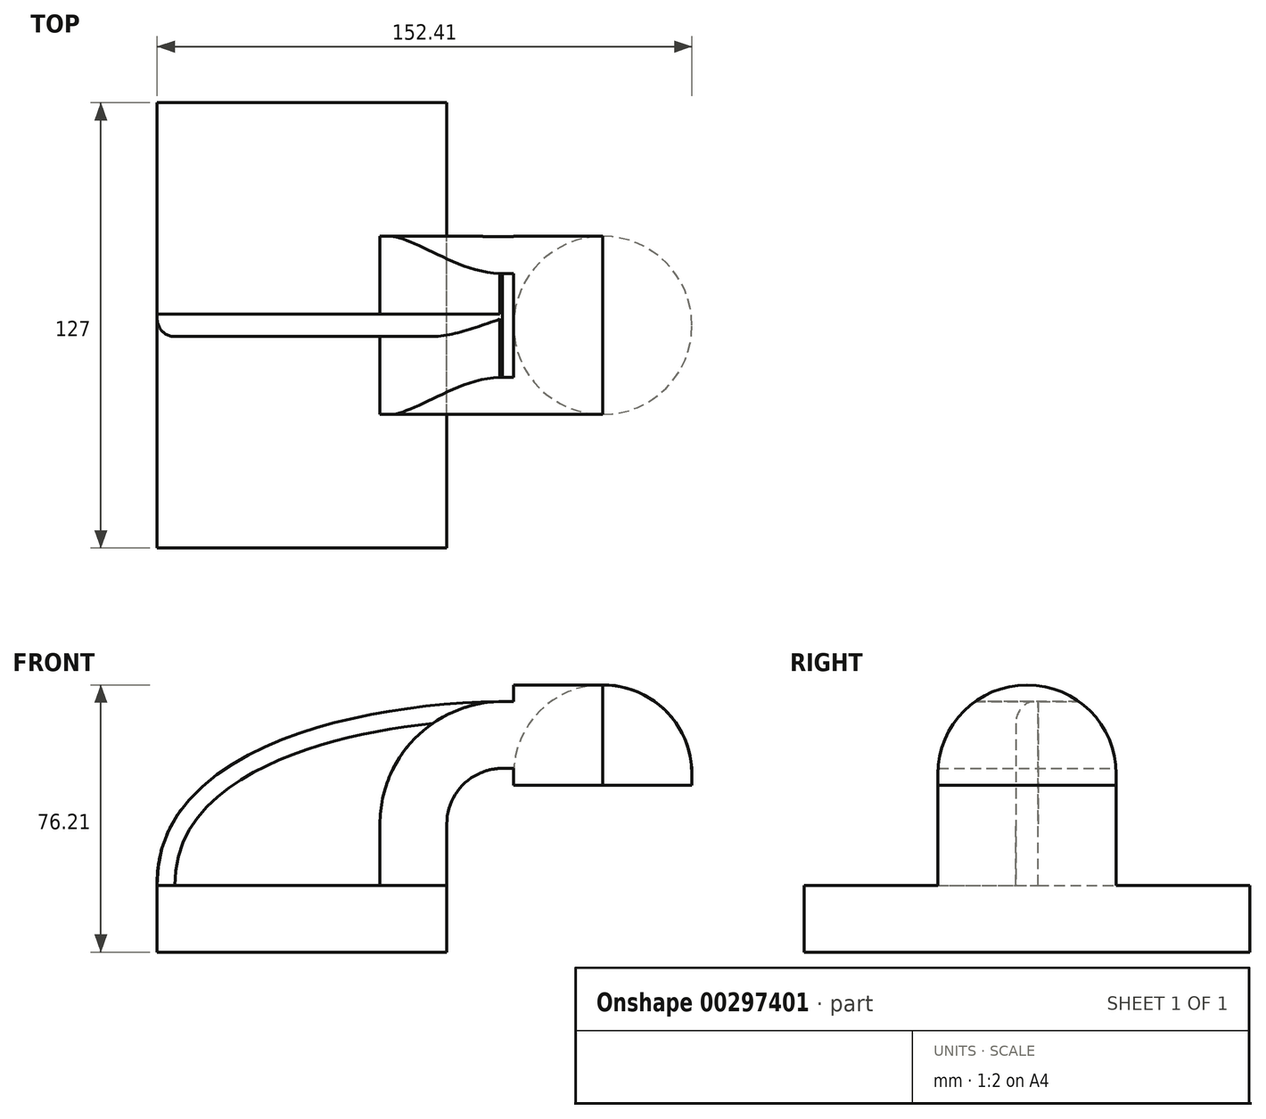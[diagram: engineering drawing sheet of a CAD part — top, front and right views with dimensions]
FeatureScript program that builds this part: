
annotation { "Feature Type Name" : "Feature", "Feature Type Description" : "" }
export const myFeature = defineFeature(function(context is Context, id is Id, definition is map)
    precondition{}
    {
        {
            var Q0;
            Q0=qCreatedBy(makeId("Front.planeOp"),FACE);
            var sketch = newSketch(context, id + "F0", { "sketchPlane" : qUnion([Q0])});
            skLineSegment(sketch, "E0.bottom", {"start": v(-41.28, 9.53) * mm, "end": v(41.28, 9.53) * mm});
            skLineSegment(sketch, "E0.top", {"start": v(-41.28, -9.52) * mm, "end": v(41.28, -9.52) * mm});
            skLineSegment(sketch, "E0.left", {"start": v(-41.28, 9.53) * mm, "end": v(-41.28, -9.52) * mm});
            skLineSegment(sketch, "E0.right", {"start": v(41.28, 9.53) * mm, "end": v(41.28, -9.52) * mm});
            skPoint(sketch, "E0.middle", {"position": v(0, 0) * mm});
            skLineSegment(sketch, "E1.bottom", {"start": v(60.33, 66.68) * mm, "end": v(111.13, 66.68) * mm});
            skLineSegment(sketch, "E1.top", {"start": v(60.33, 38.1) * mm, "end": v(111.13, 38.1) * mm});
            skLineSegment(sketch, "E1.left", {"start": v(60.33, 66.68) * mm, "end": v(60.33, 38.1) * mm});
            skLineSegment(sketch, "E1.right", {"start": v(111.13, 66.68) * mm, "end": v(111.13, 38.1) * mm});
            skPoint(sketch, "E1.middle", {"position": v(85.73, 52.39) * mm});
            skLineSegment(sketch, "E2", {"start": v(41.28, 9.53) * mm, "end": v(41.28, 27) * mm});
            skArc(sketch, "E3", {"start": v(41.28, 27) * mm, "mid": v(45.92, 38.23) * mm, "end": v(57.15, 42.88) * mm});
            skLineSegment(sketch, "E4", {"start": v(57.15, 42.88) * mm, "end": v(85.73, 42.88) * mm});
            skLineSegment(sketch, "E5.0", {"start": v(57.15, 61.93) * mm, "end": v(85.73, 61.93) * mm});
            skArc(sketch, "E5.1", {"start": v(22.23, 27) * mm, "mid": v(32.45, 51.7) * mm, "end": v(57.15, 61.93) * mm});
            skLineSegment(sketch, "E5.2", {"start": v(22.23, 9.53) * mm, "end": v(22.23, 27) * mm});
            skLineSegment(sketch, "E6", {"start": v(85.73, 38.1) * mm, "end": v(85.73, 66.68) * mm});
            skFitSpline(sketch, "E7", {"points": [v(-41.28, 9.53) * mm, v(57.15, 61.93) * mm], "startDerivative": vector(-2.03, 117.32) * mm, "endDerivative": vector(122.94, 1.14) * mm});
            skSolve(sketch);
        }
        {
            var Q0;
            Q0=makeQuery(id+"F0.imprint","IMPRINT",FACE,{"disambiguationData":[TD([[makeQuery(id+"F0.imprint","IMPRINT",EDGE,{"derivedFrom":sQuery(id+"F0.wireOp",EDGE,"E0.top")}),1.0]])]});
            extrude(context, id + "F1", {"entities" : qUnion([Q0]), "endBound" : BoundingType.SYMMETRIC, "depth" : 127 * mm});
        }
        {
            var Q0;
            {var subQ1=sQuery(id+"F0.wireOp",EDGE,"E2");Q0=makeQuery(id+"F0.imprint","IMPRINT",FACE,{"disambiguationData":[TD([[makeQuery(id+"F0.imprint","IMPRINT",EDGE,{"derivedFrom":subQ1}),1.0]])]});}
            var Q1;
            {var subQ0=sQuery(id+"F0.wireOp",EDGE,"E5.0");var subQ1=sQuery(id+"F0.wireOp",EDGE,"E1.left");var subQ2=makeQuery(id+"F0.imprint","INTERSECT",VERTEX,{"derivedFrom":[subQ1,subQ0]});Q1=makeQuery(id+"F0.imprint","IMPRINT",FACE,{"disambiguationData":[TD([[makeQuery(id+"F0.imprint","IMPRINT",EDGE,{"disambiguationData":[TD([[subQ2,-1.0]])],"derivedFrom":subQ1}),1.0]])]});}
            var Q2;
            {var subQ0=sQuery(id+"F0.wireOp",EDGE,"E1.left");var subQ1=sQuery(id+"F0.wireOp",EDGE,"E1.bottom");var subQ2=makeQuery(id+"F0.imprint","INTERSECT",VERTEX,{"derivedFrom":[subQ1,subQ0]});Q2=makeQuery(id+"F0.imprint","IMPRINT",FACE,{"disambiguationData":[TD([[makeQuery(id+"F0.imprint","IMPRINT",EDGE,{"disambiguationData":[TD([[subQ2,-1.0]])],"derivedFrom":subQ1}),-1.0]])]});}
            var Q3;
            {var subQ0=sQuery(id+"F0.wireOp",EDGE,"E1.left");var subQ1=sQuery(id+"F0.wireOp",EDGE,"E1.top");var subQ2=makeQuery(id+"F0.imprint","INTERSECT",VERTEX,{"derivedFrom":[subQ1,subQ0]});Q3=makeQuery(id+"F0.imprint","IMPRINT",FACE,{"disambiguationData":[TD([[makeQuery(id+"F0.imprint","IMPRINT",EDGE,{"disambiguationData":[TD([[subQ2,-1.0]])],"derivedFrom":subQ1}),1.0]])]});}
            extrude(context, id + "F2", {"entities" : qUnion([Q0, Q1, Q2, Q3]), "operationType" : NewBodyOperationType.ADD, "endBound" : BoundingType.SYMMETRIC, "depth" : 50.8 * mm});
        }
        {
            var Q0;
            {var subQ3=sQuery(id+"F0.wireOp",EDGE,"E5.2");Q0=makeQuery(id+"F0.imprint","IMPRINT",FACE,{"disambiguationData":[TD([[makeQuery(id+"F0.imprint","IMPRINT",EDGE,{"derivedFrom":subQ3}),1.0]])]});}
            extrude(context, id + "F3", {"entities" : qUnion([Q0]), "operationType" : NewBodyOperationType.ADD, "endBound" : BoundingType.SYMMETRIC, "depth" : 6.35 * mm});
        }
        {
            var Q0;
            {var subQ4=sQuery(id+"F0.wireOp",EDGE,"E1.right");Q0=makeQuery(id+"F0.imprint","IMPRINT",FACE,{"disambiguationData":[TD([[makeQuery(id+"F0.imprint","IMPRINT",EDGE,{"derivedFrom":subQ4}),-1.0]])]});}
            var Q1;
            Q1=sQuery(id+"F0.wireOp",EDGE,"E6");
            revolve(context, id + "F4", {"entities" : qUnion([Q0]), "axis" : qUnion([Q1]), "revolveType" : RevolveType.FULL, "oppositeDirection" : true});
        }
        {
            var Q0;
            Q0=makeQuery(id+"F4.opRevolve","SWEPT_EDGE",EDGE,{"disambiguationData":[OSD([sQuery(id+"F0.wireOp",EDGE,"E1.bottom"),sQuery(id+"F0.wireOp",EDGE,"E1.right")])]});
            fillet(context, id + "F5", {"entities" : qUnion([Q0]), "radius" : 25.4 * mm, "tangentPropagation" : true, "allowEdgeOverflow" : false});
        }
        {
            var Q0;
            Q0=makeQuery(id+"F3.opExtrude","CAP_EDGE",EDGE,{"disambiguationData":[OSD([sQuery(id+"F0.wireOp",EDGE,"E7")])],"isStart":false});
            fillet(context, id + "F6", {"entities" : qUnion([Q0]), "radius" : 5.08 * mm, "tangentPropagation" : true, "allowEdgeOverflow" : false});
        }
        {
            var Q0;
            Q0=makeQuery(id+"F2.opExtrude","CAP_EDGE",EDGE,{"disambiguationData":[OSD([sQuery(id+"F0.wireOp",EDGE,"E1.bottom")])],"isStart":false});
            fillet(context, id + "F7", {"entities" : qUnion([Q0]), "radius" : 25.4 * mm, "tangentPropagation" : true, "allowEdgeOverflow" : false});
        }
        {
            var Q0;
            Q0=makeQuery(id+"F2.opExtrude","CAP_EDGE",EDGE,{"disambiguationData":[OSD([sQuery(id+"F0.wireOp",EDGE,"E1.bottom")])],"isStart":true});
            fillet(context, id + "F8", {"entities" : qUnion([Q0]), "radius" : 25.4 * mm, "tangentPropagation" : true, "allowEdgeOverflow" : false});
        }
    });
